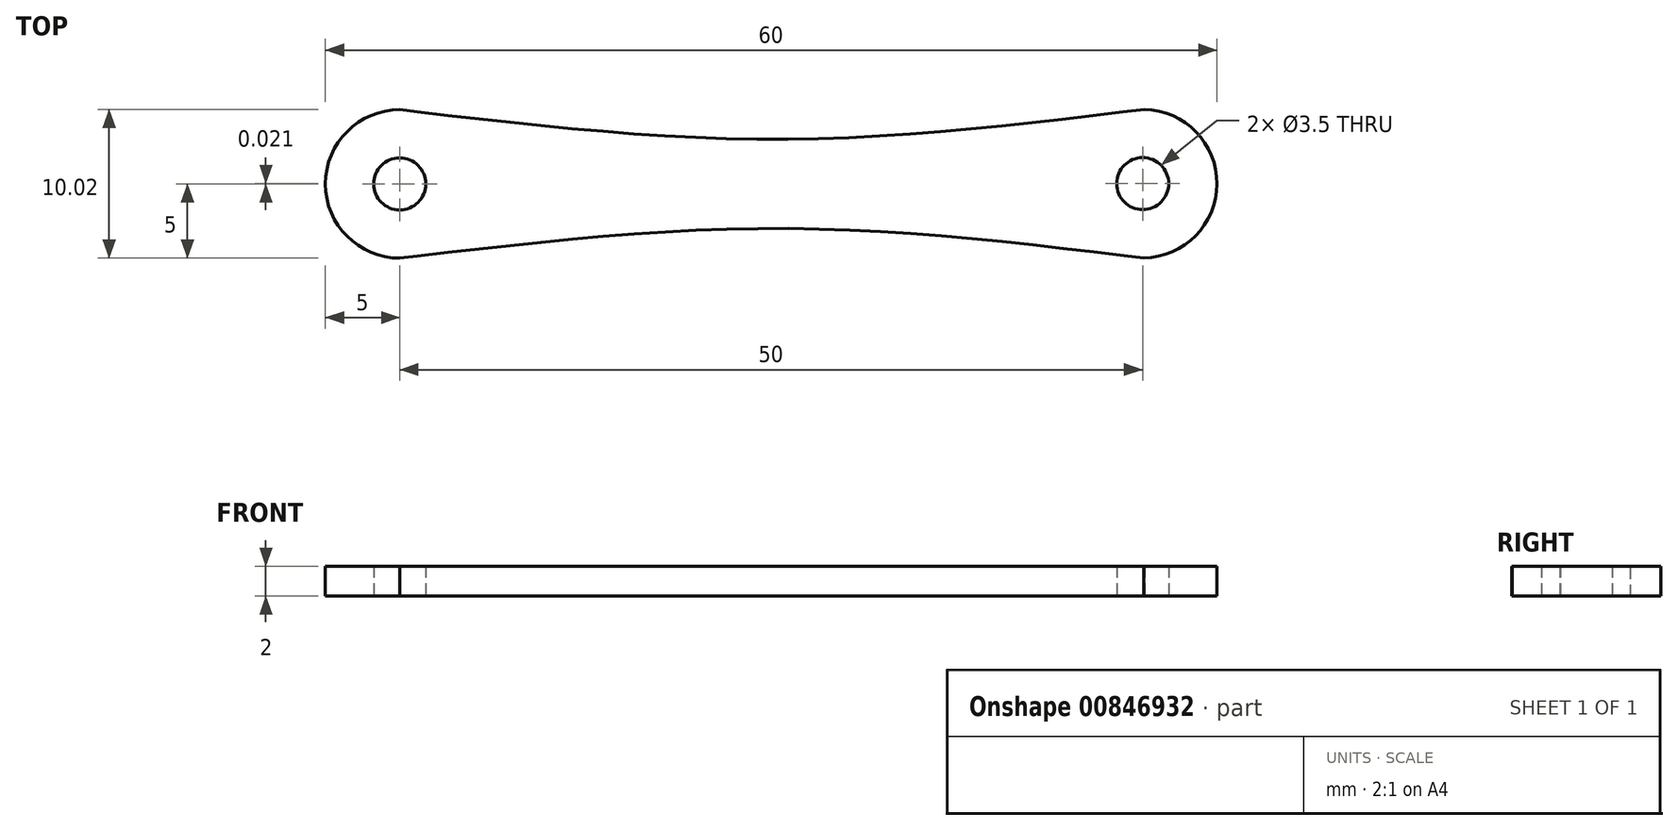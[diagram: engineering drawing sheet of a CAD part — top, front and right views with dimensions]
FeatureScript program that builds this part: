
annotation { "Feature Type Name" : "Feature", "Feature Type Description" : "" }
export const myFeature = defineFeature(function(context is Context, id is Id, definition is map)
    precondition{}
    {
        {
            var Q0;
            Q0=qCreatedBy(makeId("Top.planeOp"),FACE);
            var sketch = newSketch(context, id + "F0", { "sketchPlane" : qUnion([Q0])});
            skCircle(sketch, "E0", {"center": v(0, 0) * mm, "radius": 5 * mm});
            skCircle(sketch, "E1", {"center": v(0, 0) * mm, "radius": 1.75 * mm});
            skCircle(sketch, "E2", {"center": v(50, 0.02) * mm, "radius": 5 * mm});
            skCircle(sketch, "E3", {"center": v(50, 0.02) * mm, "radius": 1.75 * mm});
            skLineSegment(sketch, "E4", {"start": v(5, 0) * mm, "end": v(45, 0) * mm, "construction": true});
            skPoint(sketch, "E5", {"position": v(25.41, 0) * mm});
            skLineSegment(sketch, "E6", {"start": v(25.41, 3) * mm, "end": v(25.41, -3) * mm, "construction": true});
            skFitSpline(sketch, "E7", {"points": [v(0, 5) * mm, v(25.41, 3) * mm, v(50.12, 5.02) * mm], "startDerivative": vector(50.65, -5.98) * mm, "endDerivative": vector(49.6, 6.04) * mm});
            skFitSpline(sketch, "E8", {"points": [v(0, -5) * mm, v(25.41, -3) * mm, v(50.07, -4.98) * mm], "startDerivative": vector(50.64, 5.99) * mm, "endDerivative": vector(49.5, -5.97) * mm});
            skSolve(sketch);
        }
        {
            var Q0;
            Q0=makeQuery(id+"F0.imprint","IMPRINT",FACE,{"disambiguationData":[TD([[makeQuery(id+"F0.imprint","IMPRINT",EDGE,{"derivedFrom":sQuery(id+"F0.wireOp",EDGE,"E1")}),-1.0]])]});
            var Q1;
            {var subQ0=sQuery(id+"F0.wireOp",EDGE,"E7");var subQ1=sQuery(id+"F0.wireOp",EDGE,"E0");var subQ2=makeQuery(id+"F0.imprint","INTERSECT",VERTEX,{"disambiguationData":[OD(1.0)],"derivedFrom":[subQ1,subQ0]});Q1=makeQuery(id+"F0.imprint","IMPRINT",FACE,{"disambiguationData":[TD([[makeQuery(id+"F0.imprint","IMPRINT",EDGE,{"disambiguationData":[TD([[subQ2,1.0]])],"derivedFrom":subQ1}),-1.0]])]});}
            var Q2;
            Q2=makeQuery(id+"F0.imprint","IMPRINT",FACE,{"disambiguationData":[TD([[makeQuery(id+"F0.imprint","IMPRINT",EDGE,{"derivedFrom":sQuery(id+"F0.wireOp",EDGE,"E3")}),-1.0]])]});
            extrude(context, id + "F1", {"entities" : qUnion([Q0, Q1, Q2]), "depth" : 2 * mm, "offsetDistance" : 25 * mm});
        }
    });
